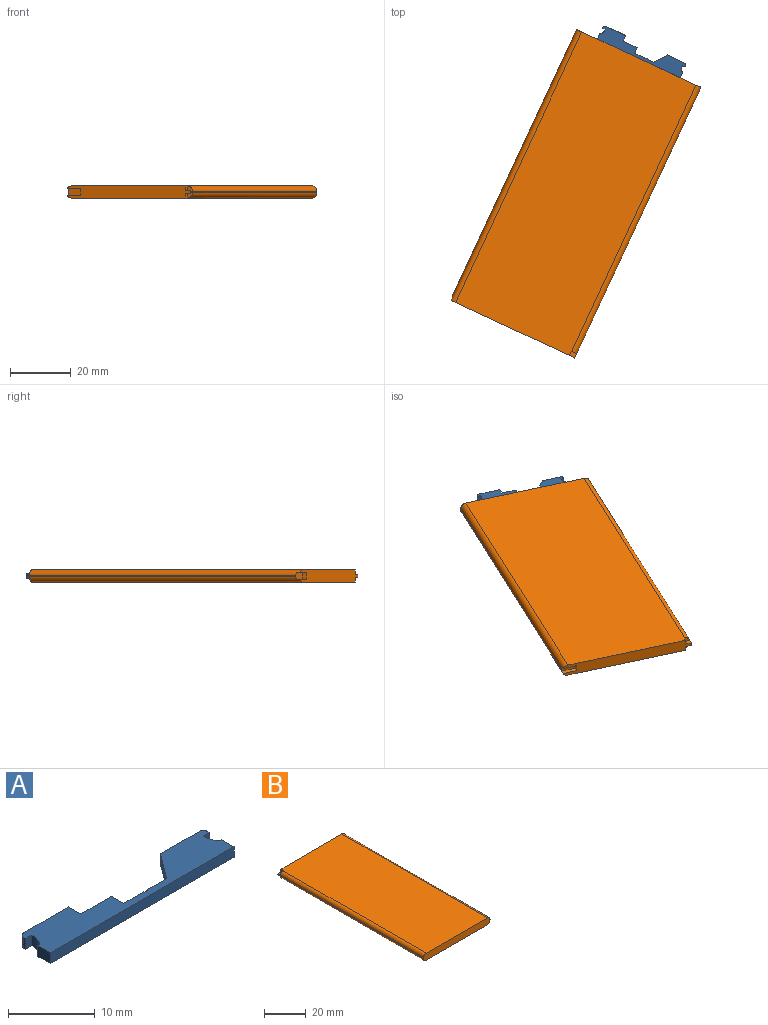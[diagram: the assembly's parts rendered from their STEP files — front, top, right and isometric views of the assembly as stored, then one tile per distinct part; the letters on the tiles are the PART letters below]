
ASSEMBLY  parts=2 mates=1
PART A: 34 faces, bbox 30x5x1.5 mm
  f0: plane 30x5mm, normal (0,0,-1), area 77.7mm2, adj f1,f3,f5,f6,f7,f8,f9,f10
  f1: plane 7.32x1.5mm, normal (0,1,0), area 9.8mm2, adj f0,f4,f10,f20,f30,f32,f33
  f2: plane 1x0.98mm, normal (0,0,-1), area 0.9mm2, adj f13,f14,f16,f21,f25
  f3: plane 3.25x1.5mm, normal (0,1,0), area 4.9mm2, adj f0,f4,f15,f24
  f4: plane 30x5mm, normal (0,0,1), area 102.6mm2, adj f1,f3,f5,f6,f7,f8,f9,f10
  f5: plane 2x1.5mm, normal (-1,0,0), area 3mm2, adj f0,f4,f12,f18
  f6: plane 2x1.5mm, normal (1,0,0), area 3mm2, adj f0,f4,f12,f17
  f7: plane 3.25x1.5mm, normal (0,1,0), area 4.9mm2, adj f0,f4,f8,f22
  f8: plane 2x1.5mm, normal (1,0,0), area 3mm2, adj f0,f4,f7,f9
  f9: plane 5x1.5mm, normal (0,1,0), area 7.5mm2, adj f0,f4,f8,f10
  f10: plane 2x1.5mm, normal (1,0,0), area 3mm2, adj f0,f1,f4,f9
  f11: plane 1.5x0.32mm, normal (-1,0,0), area 0.5mm2, adj f0,f4,f19,f20
  f12: plane 30x1.5mm, normal (0,-1,0), area 45mm2, adj f0,f4,f5,f6
  f13: plane 1.5x0.32mm, normal (1,0,0), area 0.5mm2, adj f2,f4,f16,f21
  f14: plane 6.32x1.5mm, normal (0,1,0), area 8.3mm2, adj f0,f2,f4,f15,f21,f25,f27,f28
  f15: plane 4x3mm, normal (-0.8,0.6,0), area 7.5mm2, adj f0,f3,f4,f14
  f16: plane 1.5x1mm, normal (0,-1,0), area 1.5mm2, adj f2,f4,f13,f17,f25,f27
  f17: extruded ~2x1.5mm, area 3.5mm2, adj f0,f4,f6,f16,f26,f27
  f18: extruded ~2x1.5mm, area 3.6mm2, adj f0,f4,f5,f19
  f19: plane 1.5x1mm, normal (0,-1,0), area 1.5mm2, adj f0,f4,f11,f18
  f20: cylinder r=0.68mm len=1.5mm, axis (0,0,1), area 1.6mm2, adj f0,f1,f4,f11
  f21: cylinder r=0.68mm len=1.5mm, axis (0,0,1), area 1.6mm2, adj f2,f4,f13,f14
  f22: plane 1.5x0.1mm, normal (1,0,0), area 0.2mm2, adj f0,f4,f7,f23
  f23: plane 1.5x0.5mm, normal (0,1,0), area 0.8mm2, adj f0,f4,f22,f24
  f24: plane 1.5x0.1mm, normal (-1,0,0), area 0.2mm2, adj f0,f3,f4,f23
  f25: plane 1x0.3mm, normal (-1,0,0), area 0.3mm2, adj f2,f14,f16,f27
  f26: plane 1.62x0.3mm, normal (-1,0,0), area 0.5mm2, adj f0,f17,f27,f29
  f27: plane 4x3.01mm, normal (0,0,-1), area 12mm2, adj f14,f16,f17,f25,f26,f28,f29
  f28: plane 3.01x0.3mm, normal (1,0,0), area 0.9mm2, adj f0,f14,f27,f29
  f29: plane 4x0.3mm, normal (0,1,0), area 1.2mm2, adj f0,f26,f27,f28
  f30: plane 3x0.3mm, normal (-1,0,0), area 0.9mm2, adj f0,f1,f31,f33
  f31: plane 4x0.3mm, normal (0,1,0), area 1.2mm2, adj f0,f30,f32,f33
  f32: plane 3x0.3mm, normal (1,0,0), area 0.9mm2, adj f0,f1,f31,f33
  f33: plane 4x3mm, normal (0,0,-1), area 12mm2, adj f1,f30,f31,f32
PART B: 20 faces, bbox 45x98x4 mm
  f0: plane 44.79x4mm, normal (0,1,0), area 162.6mm2, adj f2,f4,f5,f6,f7,f8,f10,f11
  f1: plane 96.5x0.28mm, normal (1,0,0), area 27mm2, adj f3,f9,f18,f19
  f2: plane 98x0.28mm, normal (-1,0,0), area 27.6mm2, adj f0,f3,f16,f17
  f3: plane 45x4mm, normal (0,-1,0), area 177mm2, adj f1,f2,f4,f5,f16,f17,f18,f19
  f4: plane 98x41.28mm, normal (0,0,1), area 4045.3mm2, adj f0,f3,f14,f15,f17,f19
  f5: plane 98x41.28mm, normal (0,0,-1), area 4045.3mm2, adj f0,f3,f11,f12,f16,f18
  f6: plane 4.79x1.5mm, normal (0,0,-1), area 7.2mm2, adj f0,f8,f9,f19
  f7: plane 4.79x1.5mm, normal (0,0,1), area 7.2mm2, adj f0,f8,f9,f18
  f8: plane 2x1.5mm, normal (1,0,0), area 3mm2, adj f0,f6,f7,f9
  f9: plane 5x2mm, normal (0,1,0), area 9.9mm2, adj f1,f6,f7,f8,f18,f19
  f10: plane 1.97x1.5mm, normal (0,0,-1), area 2.9mm2, adj f0,f11,f12,f16
  f11: plane 1.5x1.5mm, normal (-1,0,0), area 2.2mm2, adj f0,f5,f10,f12
  f12: plane 1.97x1.5mm, normal (0,1,0), area 2.3mm2, adj f5,f10,f11,f16
  f13: plane 1.97x1.5mm, normal (0,0,1), area 2.9mm2, adj f0,f14,f15,f17
  f14: plane 1.5x1.5mm, normal (-1,0,0), area 2.2mm2, adj f0,f4,f13,f15
  f15: plane 1.97x1.5mm, normal (0,1,0), area 2.3mm2, adj f4,f13,f14,f17
  f16: cylinder r=1.86mm len=98mm, axis (0,-1,0), area 282.3mm2, adj f0,f2,f3,f5,f10,f12
  f17: cylinder r=1.86mm len=98mm, axis (0,1,0), area 282.3mm2, adj f0,f2,f3,f4,f13,f15
  f18: cylinder r=1.86mm len=98mm, axis (0,1,0), area 285mm2, adj f0,f1,f3,f5,f7,f9
  f19: cylinder r=1.86mm len=98mm, axis (0,-1,0), area 285mm2, adj f0,f1,f3,f4,f6,f9
PLACE A rot(axis=(0,0,-1),25deg) t=(-26.04,-13.6,-8.57)mm
PLACE B rot(axis=(0,0,1),155deg) t=(-43.56,-51.85,-9.82)mm
MATE parallel B.f3 <-> A.f12  axis (0.42,0.91,0) through (-16.36,-19.04,-7.82)mm
